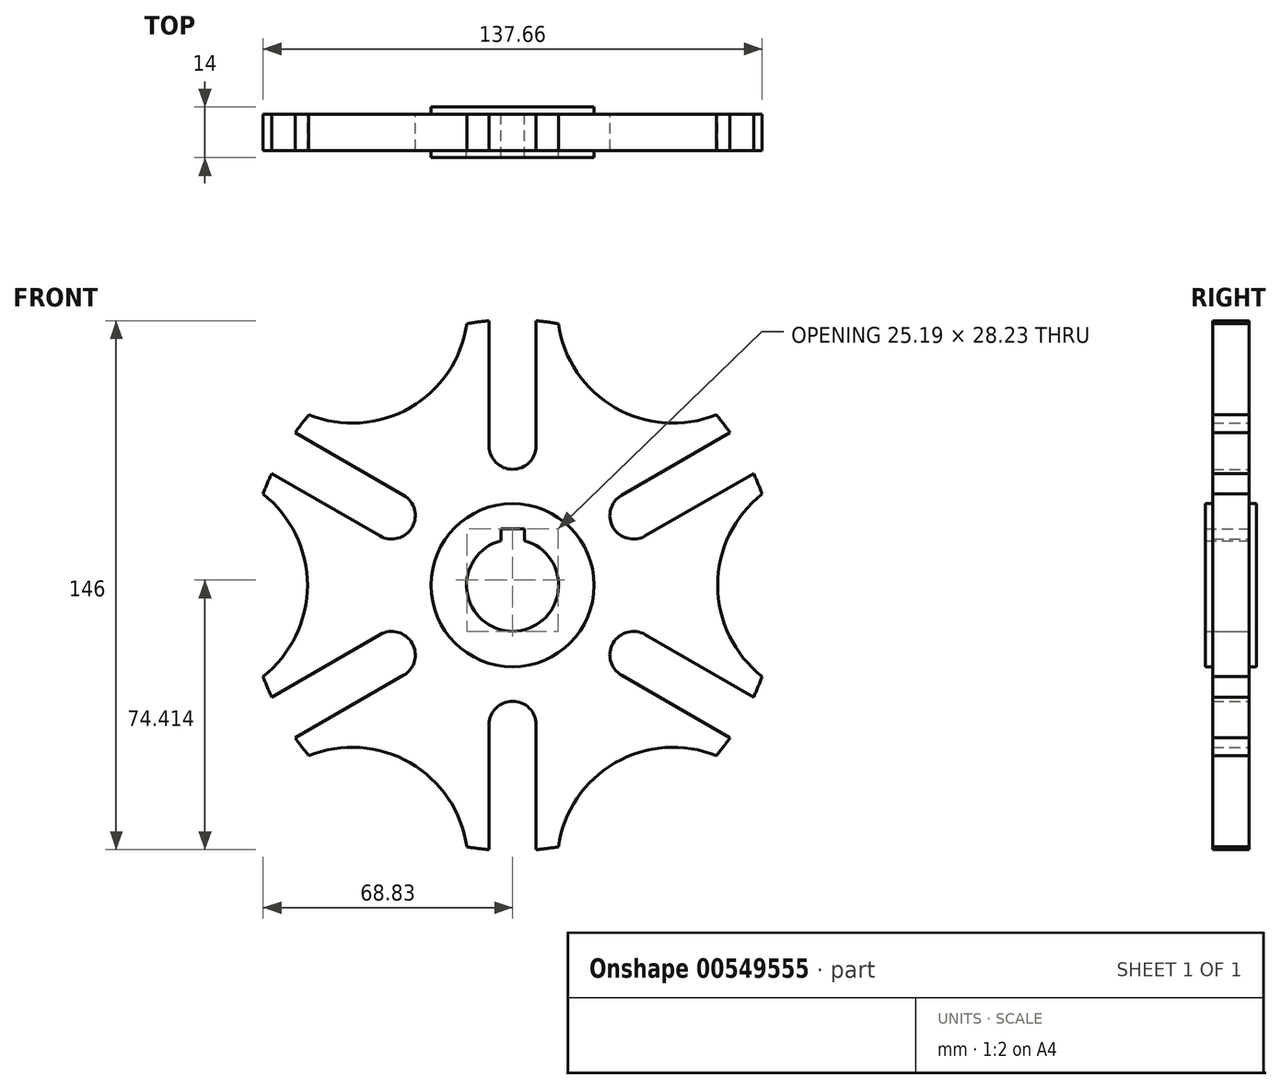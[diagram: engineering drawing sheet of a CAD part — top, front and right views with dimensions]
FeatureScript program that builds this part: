
annotation { "Feature Type Name" : "Feature", "Feature Type Description" : "" }
export const myFeature = defineFeature(function(context is Context, id is Id, definition is map)
    precondition{}
    {
        {
            var Q0;
            Q0=qCreatedBy(makeId("Front.planeOp"),FACE);
            var sketch = newSketch(context, id + "F0", { "sketchPlane" : qUnion([Q0])});
            skLineSegment(sketch, "E0", {"start": v(6.5, 38.5) * mm, "end": v(6.5, 73) * mm});
            skArc(sketch, "E1", {"start": v(12.62, 72.2) * mm, "mid": v(28.3, 49) * mm, "end": v(56.21, 47.02) * mm});
            skArc(sketch, "E2", {"start": v(0, 32) * mm, "mid": v(4.6, 33.9) * mm, "end": v(6.5, 38.5) * mm});
            skLineSegment(sketch, "E3", {"start": v(59.97, 42.13) * mm, "end": v(30.1, 24.88) * mm});
            skArc(sketch, "E4", {"start": v(30.1, 24.88) * mm, "mid": v(27.06, 20.93) * mm, "end": v(27.71, 16) * mm});
            skLineSegment(sketch, "E5", {"start": v(27.71, 16) * mm, "end": v(33.34, 19.25) * mm, "construction": true});
            skLineSegment(sketch, "E6", {"start": v(27.71, 16) * mm, "end": v(0, 0) * mm, "construction": true});
            skArc(sketch, "E7", {"start": v(12.62, 72.2) * mm, "mid": v(9.57, 72.66) * mm, "end": v(6.5, 73) * mm});
            skArc(sketch, "E8", {"start": v(59.97, 42.13) * mm, "mid": v(58.14, 44.62) * mm, "end": v(56.21, 47.02) * mm});
            skLineSegment(sketch, "E9", {"start": v(44.3, 76.72) * mm, "end": v(0, 0) * mm, "construction": true});
            skArc(sketch, "E10.1.0", {"start": v(27.71, 16) * mm, "mid": v(31.66, 12.97) * mm, "end": v(36.6, 13.62) * mm});
            skLineSegment(sketch, "E10.1.1", {"start": v(36.6, 13.62) * mm, "end": v(66.47, 30.87) * mm});
            skArc(sketch, "E10.1.2", {"start": v(68.83, 25.17) * mm, "mid": v(67.71, 28.05) * mm, "end": v(66.47, 30.87) * mm});
            skArc(sketch, "E10.1.3", {"start": v(68.83, 25.17) * mm, "mid": v(56.59, 0) * mm, "end": v(68.83, -25.17) * mm});
            skArc(sketch, "E10.1.4", {"start": v(66.47, -30.87) * mm, "mid": v(67.71, -28.05) * mm, "end": v(68.83, -25.17) * mm});
            skLineSegment(sketch, "E10.1.5", {"start": v(66.47, -30.87) * mm, "end": v(36.6, -13.62) * mm});
            skArc(sketch, "E10.1.6", {"start": v(36.6, -13.62) * mm, "mid": v(31.66, -12.97) * mm, "end": v(27.71, -16) * mm});
            skArc(sketch, "E10.2.0", {"start": v(27.71, -16) * mm, "mid": v(27.06, -20.93) * mm, "end": v(30.1, -24.88) * mm});
            skLineSegment(sketch, "E10.2.1", {"start": v(30.1, -24.88) * mm, "end": v(59.97, -42.13) * mm});
            skArc(sketch, "E10.2.2", {"start": v(56.21, -47.02) * mm, "mid": v(58.14, -44.62) * mm, "end": v(59.97, -42.13) * mm});
            skArc(sketch, "E10.2.3", {"start": v(56.21, -47.02) * mm, "mid": v(28.3, -49) * mm, "end": v(12.62, -72.2) * mm});
            skArc(sketch, "E10.2.4", {"start": v(6.5, -73) * mm, "mid": v(9.57, -72.66) * mm, "end": v(12.62, -72.2) * mm});
            skLineSegment(sketch, "E10.2.5", {"start": v(6.5, -73) * mm, "end": v(6.5, -38.5) * mm});
            skArc(sketch, "E10.2.6", {"start": v(6.5, -38.5) * mm, "mid": v(4.6, -33.9) * mm, "end": v(0, -32) * mm});
            skArc(sketch, "E10.3.0", {"start": v(0, -32) * mm, "mid": v(-4.6, -33.9) * mm, "end": v(-6.5, -38.5) * mm});
            skLineSegment(sketch, "E10.3.1", {"start": v(-6.5, -38.5) * mm, "end": v(-6.5, -73) * mm});
            skArc(sketch, "E10.3.2", {"start": v(-12.62, -72.2) * mm, "mid": v(-9.57, -72.66) * mm, "end": v(-6.5, -73) * mm});
            skArc(sketch, "E10.3.3", {"start": v(-12.62, -72.2) * mm, "mid": v(-28.3, -49) * mm, "end": v(-56.21, -47.02) * mm});
            skArc(sketch, "E10.3.4", {"start": v(-59.97, -42.13) * mm, "mid": v(-58.14, -44.62) * mm, "end": v(-56.21, -47.02) * mm});
            skLineSegment(sketch, "E10.3.5", {"start": v(-59.97, -42.13) * mm, "end": v(-30.1, -24.88) * mm});
            skArc(sketch, "E10.3.6", {"start": v(-30.1, -24.88) * mm, "mid": v(-27.06, -20.93) * mm, "end": v(-27.71, -16) * mm});
            skArc(sketch, "E10.4.0", {"start": v(-27.71, -16) * mm, "mid": v(-31.66, -12.97) * mm, "end": v(-36.6, -13.62) * mm});
            skLineSegment(sketch, "E10.4.1", {"start": v(-36.6, -13.62) * mm, "end": v(-66.47, -30.87) * mm});
            skArc(sketch, "E10.4.2", {"start": v(-68.83, -25.17) * mm, "mid": v(-67.71, -28.05) * mm, "end": v(-66.47, -30.87) * mm});
            skArc(sketch, "E10.4.3", {"start": v(-68.83, -25.17) * mm, "mid": v(-56.59, 0) * mm, "end": v(-68.83, 25.17) * mm});
            skArc(sketch, "E10.4.4", {"start": v(-66.47, 30.87) * mm, "mid": v(-67.71, 28.05) * mm, "end": v(-68.83, 25.17) * mm});
            skLineSegment(sketch, "E10.4.5", {"start": v(-66.47, 30.87) * mm, "end": v(-36.6, 13.62) * mm});
            skArc(sketch, "E10.4.6", {"start": v(-36.6, 13.62) * mm, "mid": v(-31.66, 12.97) * mm, "end": v(-27.71, 16) * mm});
            skArc(sketch, "E10.5.0", {"start": v(-27.71, 16) * mm, "mid": v(-27.06, 20.93) * mm, "end": v(-30.1, 24.88) * mm});
            skLineSegment(sketch, "E10.5.1", {"start": v(-30.1, 24.88) * mm, "end": v(-59.97, 42.13) * mm});
            skArc(sketch, "E10.5.2", {"start": v(-56.21, 47.02) * mm, "mid": v(-58.14, 44.62) * mm, "end": v(-59.97, 42.13) * mm});
            skArc(sketch, "E10.5.3", {"start": v(-56.21, 47.02) * mm, "mid": v(-28.3, 49) * mm, "end": v(-12.62, 72.2) * mm});
            skArc(sketch, "E10.5.4", {"start": v(-6.5, 73) * mm, "mid": v(-9.57, 72.66) * mm, "end": v(-12.62, 72.2) * mm});
            skLineSegment(sketch, "E10.5.5", {"start": v(-6.5, 73) * mm, "end": v(-6.5, 38.5) * mm});
            skArc(sketch, "E10.5.6", {"start": v(-6.5, 38.5) * mm, "mid": v(-4.6, 33.9) * mm, "end": v(0, 32) * mm});
            skLineSegment(sketch, "E10.anchor1", {"start": v(0, 0) * mm, "end": v(0, 32) * mm, "construction": true});
            skLineSegment(sketch, "E10.anchor2", {"start": v(0, 0) * mm, "end": v(-27.71, 16) * mm, "construction": true});
            skSolve(sketch);
        }
        {
            var Q0;
            Q0 = qSketchRegion(id + "F0", true);
            extrude(context, id + "F1", {"entities" : qUnion([Q0]), "endBound" : BoundingType.SYMMETRIC, "depth" : 10 * mm, "offsetDistance" : 25 * mm});
        }
        {
            var Q0;
            Q0=qCreatedBy(makeId("Front.planeOp"),FACE);
            var sketch = newSketch(context, id + "F2", { "sketchPlane" : qUnion([Q0])});
            skCircle(sketch, "E11", {"center": v(0, 0) * mm, "radius": 22.5 * mm});
            skSolve(sketch);
        }
        {
            var Q0;
            Q0 = qSketchRegion(id + "F2", true);
            extrude(context, id + "F3", {"entities" : qUnion([Q0]), "operationType" : NewBodyOperationType.ADD, "endBound" : BoundingType.SYMMETRIC, "depth" : 14 * mm, "offsetDistance" : 25 * mm});
        }
        {
            var Q0;
            Q0=qCreatedBy(makeId("Front.planeOp"),FACE);
            var sketch = newSketch(context, id + "F4", { "sketchPlane" : qUnion([Q0])});
            skCircle(sketch, "E12", {"center": v(0, 0) * mm, "radius": 12.7 * mm});
            skLineSegment(sketch, "E13.bottom", {"start": v(-3.25, 12.28) * mm, "end": v(3.25, 12.28) * mm});
            skLineSegment(sketch, "E13.top", {"start": v(-3.25, 15.53) * mm, "end": v(3.25, 15.53) * mm});
            skLineSegment(sketch, "E13.left", {"start": v(-3.25, 12.28) * mm, "end": v(-3.25, 15.53) * mm});
            skLineSegment(sketch, "E13.right", {"start": v(3.25, 12.28) * mm, "end": v(3.25, 15.53) * mm});
            skSolve(sketch);
        }
        {
            var Q0;
            Q0 = qSketchRegion(id + "F4", true);
            extrude(context, id + "F5", {"entities" : qUnion([Q0]), "operationType" : NewBodyOperationType.REMOVE, "endBound" : BoundingType.SYMMETRIC, "depth" : 25 * mm, "offsetDistance" : 25 * mm});
        }
    });
